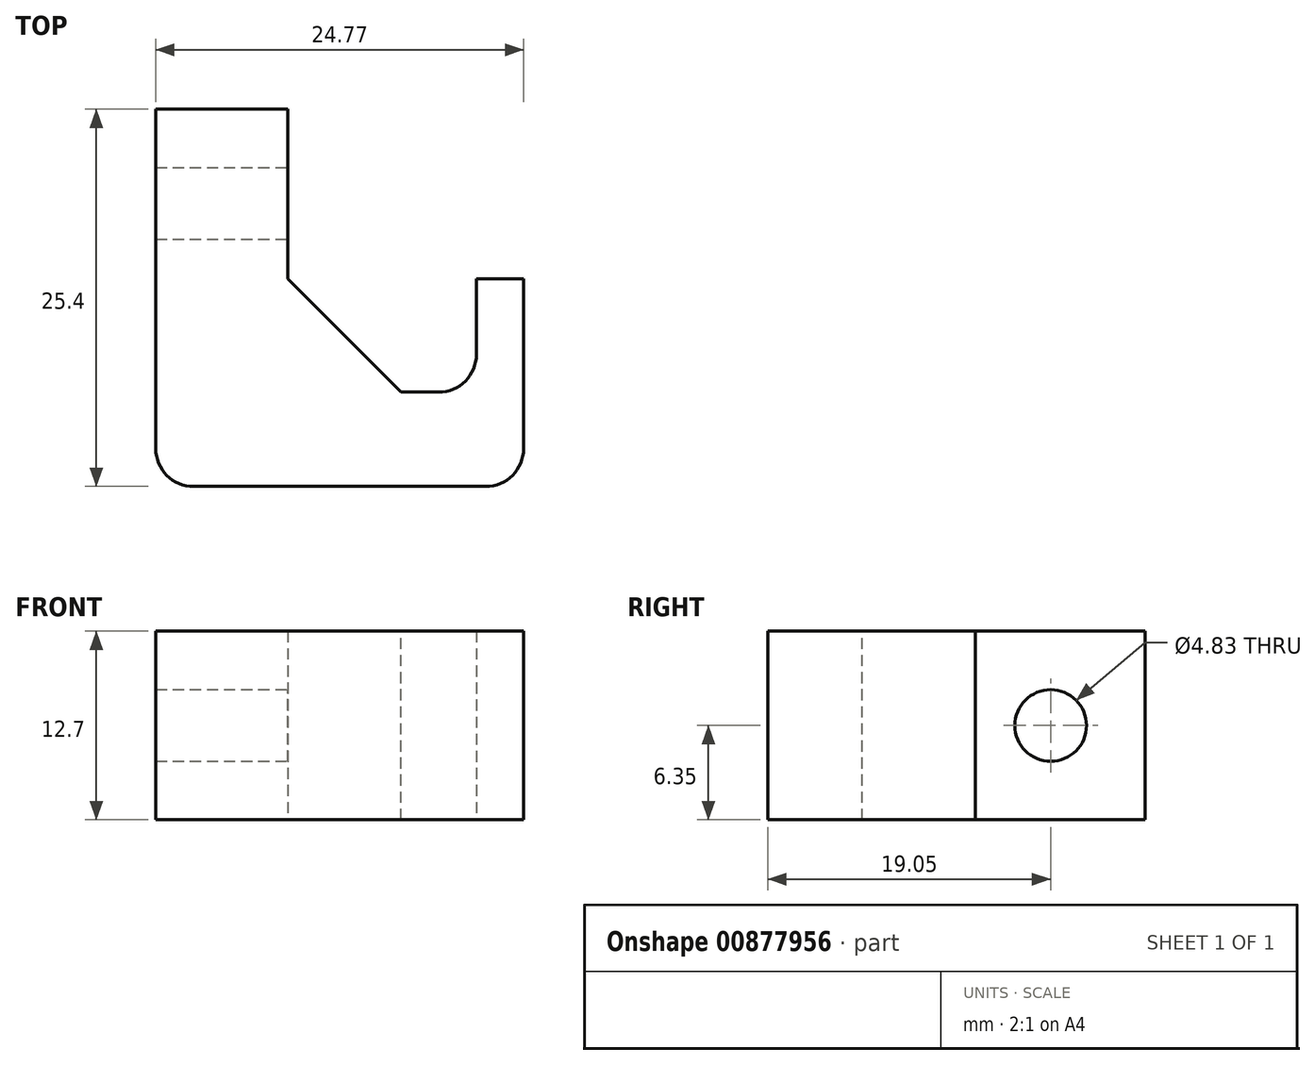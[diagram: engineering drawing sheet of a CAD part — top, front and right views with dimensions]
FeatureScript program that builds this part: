
annotation { "Feature Type Name" : "Feature", "Feature Type Description" : "" }
export const myFeature = defineFeature(function(context is Context, id is Id, definition is map)
    precondition{}
    {
        {
            var Q0;
            Q0=qCreatedBy(makeId("Top.planeOp"),FACE);
            var sketch = newSketch(context, id + "F0", { "sketchPlane" : qUnion([Q0])});
            skLineSegment(sketch, "E0.bottom", {"start": v(-14.94, 19.05) * mm, "end": v(-6.05, 19.05) * mm});
            skLineSegment(sketch, "E0.top", {"start": v(-14.94, 0) * mm, "end": v(-6.05, 0) * mm});
            skLineSegment(sketch, "E0.left", {"start": v(-14.94, 19.05) * mm, "end": v(-14.94, 0) * mm});
            skLineSegment(sketch, "E0.right", {"start": v(-6.05, 19.05) * mm, "end": v(-6.05, 0) * mm});
            skLineSegment(sketch, "E1.bottom", {"start": v(6.65, 0) * mm, "end": v(9.83, 0) * mm});
            skLineSegment(sketch, "E1.top", {"start": v(6.65, 7.62) * mm, "end": v(9.83, 7.62) * mm});
            skLineSegment(sketch, "E1.left", {"start": v(6.65, 0) * mm, "end": v(6.65, 7.62) * mm});
            skLineSegment(sketch, "E1.right", {"start": v(9.83, 0) * mm, "end": v(9.83, 7.62) * mm});
            skLineSegment(sketch, "E2.bottom", {"start": v(-14.94, 0) * mm, "end": v(9.83, 0) * mm});
            skLineSegment(sketch, "E2.top", {"start": v(-14.94, -6.35) * mm, "end": v(9.83, -6.35) * mm});
            skLineSegment(sketch, "E2.left", {"start": v(-14.94, 0) * mm, "end": v(-14.94, -6.35) * mm});
            skLineSegment(sketch, "E2.right", {"start": v(9.83, 0) * mm, "end": v(9.83, -6.35) * mm});
            skSolve(sketch);
        }
        {
            var Q0;
            Q0 = qSketchRegion(id + "F0", true);
            extrude(context, id + "F1", {"entities" : qUnion([Q0]), "depth" : 12.7 * mm, "offsetDistance" : 25.4 * mm});
        }
        {
            var Q0;
            Q0=makeQuery(id+"F1.opExtrude","SWEPT_EDGE",EDGE,{"disambiguationData":[OSD([sQuery(id+"F0.wireOp",EDGE,"E1.left"),sQuery(id+"F0.wireOp",EDGE,"E2.bottom")])]});
            var Q1;
            Q1=makeQuery(id+"F1.opExtrude","SWEPT_EDGE",EDGE,{"disambiguationData":[OSD([sQuery(id+"F0.wireOp",EDGE,"E2.top"),sQuery(id+"F0.wireOp",EDGE,"E2.right")])]});
            var Q2;
            Q2=makeQuery(id+"F1.opExtrude","SWEPT_EDGE",EDGE,{"disambiguationData":[OSD([sQuery(id+"F0.wireOp",EDGE,"E2.top"),sQuery(id+"F0.wireOp",EDGE,"E2.left")])]});
            fillet(context, id + "F2", {"entities" : qUnion([Q0, Q1, Q2]), "radius" : 2.54 * mm, "tangentPropagation" : true, "allowEdgeOverflow" : false});
        }
        {
            var Q0;
            Q0=makeQuery(id+"F1.opExtrude","SWEPT_FACE",FACE,{"disambiguationData":[OSD([sQuery(id+"F0.wireOp",EDGE,"E0.right")])]});
            var sketch = newSketch(context, id + "F3", { "sketchPlane" : qUnion([Q0])});
            skCircle(sketch, "E3", {"center": v(12.7, 6.35) * mm, "radius": 2.41 * mm});
            skPoint(sketch, "E3.centerSnap0", {"position": v(19.05, 6.35) * mm});
            skSolve(sketch);
        }
        {
            var Q0;
            Q0=makeQuery(id+"F3.imprint","IMPRINT",FACE,{"disambiguationData":[TD([[makeQuery(id+"F3.imprint","IMPRINT",EDGE,{"derivedFrom":sQuery(id+"F3.wireOp",EDGE,"E3")}),1.0]])]});
            extrude(context, id + "F4", {"entities" : qUnion([Q0]), "operationType" : NewBodyOperationType.REMOVE, "oppositeDirection" : true, "depth" : 25.4 * mm, "offsetDistance" : 25.4 * mm});
        }
        {
            var Q0;
            Q0=makeQuery(id+"F1.opExtrude","SWEPT_EDGE",EDGE,{"disambiguationData":[OSD([sQuery(id+"F0.wireOp",EDGE,"E0.right"),sQuery(id+"F0.wireOp",EDGE,"E2.bottom")])]});
            chamfer(context, id + "F5", {"entities" : qUnion([Q0]), "width" : 7.62 * mm, "tangentPropagation" : true});
        }
    });
